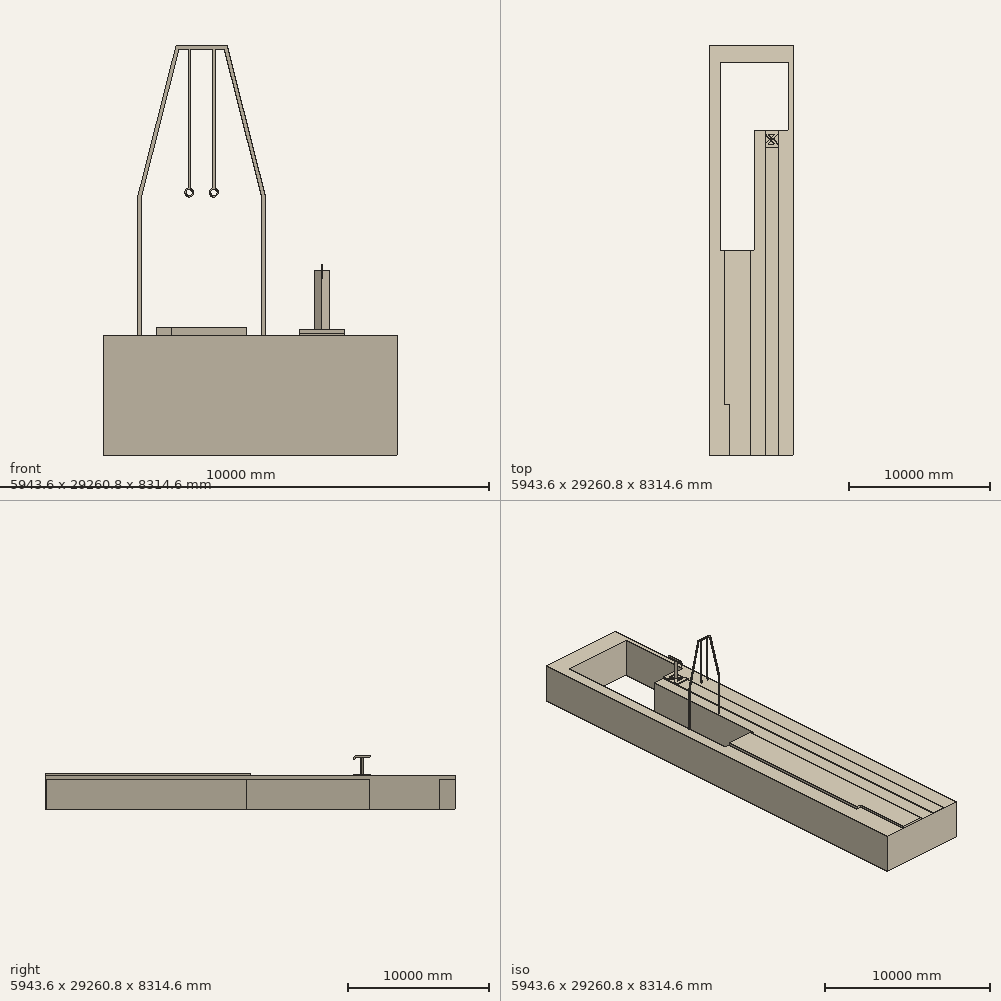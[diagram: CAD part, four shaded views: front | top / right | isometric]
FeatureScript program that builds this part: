
annotation { "Feature Type Name" : "Feature", "Feature Type Description" : "" }
export const myFeature = defineFeature(function(context is Context, id is Id, definition is map)
    precondition{}
    {
        {
            var Q0;
            Q0=qCreatedBy(makeId("Top.planeOp"),FACE);
            var sketch = newSketch(context, id + "F0", { "sketchPlane" : qUnion([Q0])});
            skLineSegment(sketch, "E0.bottom", {"start": v(-10972.8, 14630.4) * mm, "end": v(10972.8, 14630.4) * mm});
            skLineSegment(sketch, "E0.top", {"start": v(-10972.8, -14630.4) * mm, "end": v(10972.8, -14630.4) * mm});
            skLineSegment(sketch, "E0.left", {"start": v(-10972.8, 14630.4) * mm, "end": v(-10972.8, -14630.4) * mm});
            skLineSegment(sketch, "E0.right", {"start": v(10972.8, 14630.4) * mm, "end": v(10972.8, -14630.4) * mm});
            skPoint(sketch, "E0.middle", {"position": v(0, 0) * mm});
            skLineSegment(sketch, "E1", {"start": v(-10210.8, -14630.4) * mm, "end": v(-10210.8, 14630.4) * mm});
            skLineSegment(sketch, "E2", {"start": v(-7772.4, 0) * mm, "end": v(-7772.4, -14630.4) * mm});
            skLineSegment(sketch, "E3", {"start": v(-7010.4, -14630.4) * mm, "end": v(-7010.4, 0) * mm});
            skLineSegment(sketch, "E4", {"start": v(-7772.4, 0) * mm, "end": v(-9601.2, 0) * mm});
            skLineSegment(sketch, "E5", {"start": v(-9601.2, 0) * mm, "end": v(-9601.2, -10972.8) * mm});
            skLineSegment(sketch, "E6", {"start": v(-9601.2, -10972.8) * mm, "end": v(-8991.6, -10972.8) * mm});
            skLineSegment(sketch, "E7", {"start": v(-8991.6, -10972.8) * mm, "end": v(-8991.6, -14630.4) * mm});
            skLineSegment(sketch, "E8.bottom", {"start": v(-5334, 8534.4) * mm, "end": v(-7772.4, 8534.4) * mm});
            skLineSegment(sketch, "E8.top", {"start": v(-5334, 13411.2) * mm, "end": v(-7772.4, 13411.2) * mm});
            skLineSegment(sketch, "E8.left", {"start": v(-5334, 8534.4) * mm, "end": v(-5334, 13411.2) * mm});
            skLineSegment(sketch, "E8.right", {"start": v(-7772.4, 8534.4) * mm, "end": v(-7772.4, 13411.2) * mm});
            skPoint(sketch, "E8.middle", {"position": v(-6553.2, 10972.8) * mm});
            skLineSegment(sketch, "E9", {"start": v(-7772.4, 8534.4) * mm, "end": v(-7772.4, 0) * mm});
            skLineSegment(sketch, "E10", {"start": v(-5334, 8534.4) * mm, "end": v(-5334, -14630.4) * mm});
            skLineSegment(sketch, "E11", {"start": v(-5029.2, 14630.4) * mm, "end": v(-5029.2, -14630.4) * mm});
            skLineSegment(sketch, "E12", {"start": v(-6553.2, 8534.4) * mm, "end": v(-6553.2, -14630.4) * mm, "construction": true});
            skLineSegment(sketch, "E13", {"start": v(-6096, 8534.4) * mm, "end": v(-6096, -14630.4) * mm, "construction": true});
            skLineSegment(sketch, "E14", {"start": v(-7010.4, 8534.4) * mm, "end": v(-7010.4, -14630.4) * mm, "construction": true});
            skLineSegment(sketch, "E15", {"start": v(-10210.8, 3048) * mm, "end": v(-7772.4, 3048) * mm, "construction": true});
            skLineSegment(sketch, "E16", {"start": v(-10210.8, 5486.4) * mm, "end": v(-7772.4, 5486.4) * mm, "construction": true});
            skSolve(sketch);
        }
        {
            var Q0;
            Q0=qCreatedBy(makeId("Top.planeOp"),FACE);
            var sketch = newSketch(context, id + "F1", { "sketchPlane" : qUnion([Q0])});
            skLineSegment(sketch, "E17", {"start": v(-5029.2, -14630.4) * mm, "end": v(-5029.2, 14630.4) * mm});
            skLineSegment(sketch, "E18", {"start": v(-5029.2, 14630.4) * mm, "end": v(-10972.8, 14630.4) * mm});
            skLineSegment(sketch, "E19", {"start": v(-10972.8, 14630.4) * mm, "end": v(-10972.8, -14630.4) * mm});
            skLineSegment(sketch, "E20", {"start": v(-10972.8, -14630.4) * mm, "end": v(-5029.2, -14630.4) * mm});
            skLineSegment(sketch, "E21", {"start": v(-5334, 13411.2) * mm, "end": v(-5334, 8534.4) * mm});
            skLineSegment(sketch, "E22", {"start": v(-5334, 8534.4) * mm, "end": v(-7772.4, 8534.4) * mm});
            skLineSegment(sketch, "E23", {"start": v(-7772.4, 8534.4) * mm, "end": v(-7772.4, 0) * mm});
            skLineSegment(sketch, "E24", {"start": v(-7772.4, 0) * mm, "end": v(-10210.8, 0) * mm});
            skLineSegment(sketch, "E25", {"start": v(-10210.8, 0) * mm, "end": v(-10210.8, 13411.2) * mm});
            skLineSegment(sketch, "E26", {"start": v(-10210.8, 13411.2) * mm, "end": v(-5334, 13411.2) * mm});
            skSolve(sketch);
        }
        {
            var Q0;
            Q0 = qSketchRegion(id + "F1", true);
            extrude(context, id + "F2", {"entities" : qUnion([Q0]), "depth" : 2438.4 * mm});
        }
        {
            var Q0;
            Q0=makeQuery(id+"F2.opExtrude","SWEPT_FACE",FACE,{"disambiguationData":[OSD([sQuery(id+"F1.wireOp",EDGE,"E17")])]});
            var sketch = newSketch(context, id + "F3", { "sketchPlane" : qUnion([Q0])});
            skLineSegment(sketch, "E27.0", {"start": v(13411.2, 2438.4) * mm, "end": v(13411.2, 0) * mm, "construction": true});
            skLineSegment(sketch, "E28.0", {"start": v(8534.4, 2438.4) * mm, "end": v(8534.4, 0) * mm, "construction": true});
            skLineSegment(sketch, "E29.bottom", {"start": v(14630.4, 2133.6) * mm, "end": v(13462, 2133.6) * mm});
            skLineSegment(sketch, "E29.top", {"start": v(14630.4, 0) * mm, "end": v(13462, 0) * mm});
            skLineSegment(sketch, "E29.left", {"start": v(14630.4, 2133.6) * mm, "end": v(14630.4, 0) * mm});
            skLineSegment(sketch, "E29.right", {"start": v(13462, 2133.6) * mm, "end": v(13462, 0) * mm});
            skLineSegment(sketch, "E30.bottom", {"start": v(8483.6, 0) * mm, "end": v(-14528.8, 0) * mm});
            skLineSegment(sketch, "E30.top", {"start": v(8483.6, 2133.6) * mm, "end": v(-14528.8, 2133.6) * mm});
            skLineSegment(sketch, "E30.left", {"start": v(8483.6, 0) * mm, "end": v(8483.6, 2133.6) * mm});
            skLineSegment(sketch, "E30.right", {"start": v(-14528.8, 0) * mm, "end": v(-14528.8, 2133.6) * mm});
            skSolve(sketch);
        }
        {
            var Q0;
            Q0 = qSketchRegion(id + "F3", true);
            extrude(context, id + "F4", {"entities" : qUnion([Q0]), "operationType" : NewBodyOperationType.REMOVE, "oppositeDirection" : true, "depth" : 2362.2 * mm});
        }
        {
            var Q0;
            Q0=makeQuery(id+"F4.boolean.opBoolean","COPY",FACE,{"derivedFrom":makeQuery(id+"F4.opExtrude","CAP_FACE",FACE,{"disambiguationData":[OSD([sQuery(id+"F3.wireOp",EDGE,"E30.bottom"),sQuery(id+"F3.wireOp",EDGE,"E30.top"),sQuery(id+"F3.wireOp",EDGE,"E30.left"),sQuery(id+"F3.wireOp",EDGE,"E30.right")])],"isStart":false})});
            var sketch = newSketch(context, id + "F5", { "sketchPlane" : qUnion([Q0])});
            skLineSegment(sketch, "E31.bottom", {"start": v(-14528.8, 2133.6) * mm, "end": v(-304.8, 2133.6) * mm});
            skLineSegment(sketch, "E31.top", {"start": v(-14528.8, 0) * mm, "end": v(-304.8, 0) * mm});
            skLineSegment(sketch, "E31.left", {"start": v(-14528.8, 2133.6) * mm, "end": v(-14528.8, 0) * mm});
            skLineSegment(sketch, "E31.right", {"start": v(-304.8, 2133.6) * mm, "end": v(-304.8, 0) * mm});
            skSolve(sketch);
        }
        {
            var Q0;
            Q0 = qSketchRegion(id + "F5", true);
            extrude(context, id + "F6", {"entities" : qUnion([Q0]), "operationType" : NewBodyOperationType.REMOVE, "oppositeDirection" : true, "depth" : 2743.2 * mm});
        }
        {
            var Q0;
            Q0=makeQuery(id+"F2.opExtrude","CAP_FACE",FACE,{"disambiguationData":[OSD([sQuery(id+"F1.wireOp",EDGE,"E17"),sQuery(id+"F1.wireOp",EDGE,"E18"),sQuery(id+"F1.wireOp",EDGE,"E19"),sQuery(id+"F1.wireOp",EDGE,"E20"),sQuery(id+"F1.wireOp",EDGE,"E21"),sQuery(id+"F1.wireOp",EDGE,"E22"),sQuery(id+"F1.wireOp",EDGE,"E23"),sQuery(id+"F1.wireOp",EDGE,"E24"),sQuery(id+"F1.wireOp",EDGE,"E25"),sQuery(id+"F1.wireOp",EDGE,"E26")])],"isStart":false});
            var sketch = newSketch(context, id + "F7", { "sketchPlane" : qUnion([Q0])});
            skLineSegment(sketch, "E32.bottom", {"start": v(-7010.4, 8534.4) * mm, "end": v(-6096, 8534.4) * mm});
            skLineSegment(sketch, "E32.top", {"start": v(-7010.4, -14630.4) * mm, "end": v(-6096, -14630.4) * mm});
            skLineSegment(sketch, "E32.left", {"start": v(-7010.4, 8534.4) * mm, "end": v(-7010.4, -14630.4) * mm});
            skLineSegment(sketch, "E32.right", {"start": v(-6096, 8534.4) * mm, "end": v(-6096, -14630.4) * mm});
            skSolve(sketch);
        }
        {
            var Q0;
            Q0 = qSketchRegion(id + "F7", true);
            extrude(context, id + "F8", {"entities" : qUnion([Q0]), "depth" : 34.92 * mm});
        }
        {
            var Q0;
            Q0=makeQuery(id+"F8.opExtrude","CAP_FACE",FACE,{"disambiguationData":[OSD([sQuery(id+"F7.wireOp",EDGE,"E32.bottom"),sQuery(id+"F7.wireOp",EDGE,"E32.top"),sQuery(id+"F7.wireOp",EDGE,"E32.left"),sQuery(id+"F7.wireOp",EDGE,"E32.right")])],"isStart":false});
            var sketch = newSketch(context, id + "F9", { "sketchPlane" : qUnion([Q0])});
            skLineSegment(sketch, "E33.bottom", {"start": v(-7010.4, 8534.4) * mm, "end": v(-6096, 8534.4) * mm});
            skLineSegment(sketch, "E33.top", {"start": v(-7010.4, 7334.4) * mm, "end": v(-6096, 7334.4) * mm});
            skLineSegment(sketch, "E33.left", {"start": v(-7010.4, 8534.4) * mm, "end": v(-7010.4, 8302.15) * mm});
            skLineSegment(sketch, "E33.right", {"start": v(-6096, 8534.4) * mm, "end": v(-6096, 8302.15) * mm});
            skLineSegment(sketch, "E34", {"start": v(-7010.4, 8302.15) * mm, "end": v(-6698.52, 7934.4) * mm});
            skPoint(sketch, "E34.endSnap0", {"position": v(-6096, 7934.4) * mm});
            skLineSegment(sketch, "E35", {"start": v(-6698.52, 7934.4) * mm, "end": v(-7010.4, 7566.65) * mm});
            skLineSegment(sketch, "E36", {"start": v(-6096, 8302.15) * mm, "end": v(-6407.88, 7934.4) * mm});
            skLineSegment(sketch, "E37", {"start": v(-6407.88, 7934.4) * mm, "end": v(-6096, 7566.65) * mm});
            skLineSegment(sketch, "E38", {"start": v(-6698.52, 7934.4) * mm, "end": v(-7010.4, 7934.4) * mm, "construction": true});
            skLineSegment(sketch, "E39", {"start": v(-6407.88, 7934.4) * mm, "end": v(-6096, 7934.4) * mm, "construction": true});
            skLineSegment(sketch, "E40", {"start": v(-6826.71, 7566.65) * mm, "end": v(-6302.47, 7566.65) * mm});
            skLineSegment(sketch, "E41", {"start": v(-6302.47, 7566.65) * mm, "end": v(-6564.6, 7828.77) * mm});
            skLineSegment(sketch, "E42", {"start": v(-6564.6, 7828.77) * mm, "end": v(-6826.71, 7566.65) * mm});
            skLineSegment(sketch, "E43", {"start": v(-6826.71, 8302.15) * mm, "end": v(-6564.6, 8040.03) * mm});
            skLineSegment(sketch, "E44", {"start": v(-6564.6, 8040.03) * mm, "end": v(-6302.47, 8302.15) * mm});
            skLineSegment(sketch, "E45", {"start": v(-6302.47, 8302.15) * mm, "end": v(-6826.71, 8302.15) * mm});
            skLineSegment(sketch, "E46.trimOffspring", {"start": v(-7010.4, 7566.65) * mm, "end": v(-7010.4, 7334.4) * mm});
            skLineSegment(sketch, "E47.trimOffspring", {"start": v(-6096, 7566.65) * mm, "end": v(-6096, 7334.4) * mm});
            skSolve(sketch);
        }
        {
            var Q0;
            Q0 = qSketchRegion(id + "F9", true);
            extrude(context, id + "F10", {"entities" : qUnion([Q0]), "depth" : 76.2 * mm});
        }
        {
            var Q0;
            Q0=makeQuery(id+"F10.opExtrude","CAP_FACE",FACE,{"disambiguationData":[OSD([sQuery(id+"F9.wireOp",EDGE,"E33.bottom"),sQuery(id+"F9.wireOp",EDGE,"E33.top"),sQuery(id+"F9.wireOp",EDGE,"E33.left"),sQuery(id+"F9.wireOp",EDGE,"E33.right"),sQuery(id+"F9.wireOp",EDGE,"E34"),sQuery(id+"F9.wireOp",EDGE,"E35"),sQuery(id+"F9.wireOp",EDGE,"E36"),sQuery(id+"F9.wireOp",EDGE,"E37"),sQuery(id+"F9.wireOp",EDGE,"E40"),sQuery(id+"F9.wireOp",EDGE,"E41"),sQuery(id+"F9.wireOp",EDGE,"E42"),sQuery(id+"F9.wireOp",EDGE,"E43"),sQuery(id+"F9.wireOp",EDGE,"E44"),sQuery(id+"F9.wireOp",EDGE,"E45"),sQuery(id+"F9.wireOp",EDGE,"E46.trimOffspring"),sQuery(id+"F9.wireOp",EDGE,"E47.trimOffspring")])],"isStart":false});
            var sketch = newSketch(context, id + "F11", { "sketchPlane" : qUnion([Q0])});
            skLineSegment(sketch, "E48", {"start": v(-6698.52, 7934.4) * mm, "end": v(-6564.6, 8040.03) * mm});
            skLineSegment(sketch, "E49", {"start": v(-6564.6, 8040.03) * mm, "end": v(-6407.88, 7934.4) * mm});
            skLineSegment(sketch, "E50", {"start": v(-6407.88, 7934.4) * mm, "end": v(-6564.6, 7828.77) * mm});
            skLineSegment(sketch, "E51", {"start": v(-6564.6, 7828.77) * mm, "end": v(-6698.52, 7934.4) * mm});
            skSolve(sketch);
        }
        {
            var Q0;
            Q0 = qSketchRegion(id + "F11", true);
            extrude(context, id + "F12", {"entities" : qUnion([Q0]), "operationType" : NewBodyOperationType.ADD, "depth" : 1200 * mm});
        }
        {
            var Q0;
            Q0=makeQuery(id+"F10.opExtrude","SWEPT_FACE",FACE,{"disambiguationData":[OSD([sQuery(id+"F9.wireOp",EDGE,"E33.left")])]});
            var Q1;
            Q1=makeQuery(id+"F10.opExtrude","SWEPT_FACE",FACE,{"disambiguationData":[OSD([sQuery(id+"F9.wireOp",EDGE,"E33.right")])]});
            cPlane(context, id + "F13", {"entities" : qUnion([Q0, Q1]), "cplaneType" : CPlaneType.MID_PLANE, "offset" : 25.4 * mm, "width" : 152.4 * mm, "height" : 152.4 * mm});
        }
        {
            var Q0;
            Q0=qCreatedBy(id+"F13.planeOp",FACE);
            var sketch = newSketch(context, id + "F14", { "sketchPlane" : qUnion([Q0])});
            skLineSegment(sketch, "E52", {"start": v(-8534.4, 3749.53) * mm, "end": v(-7652.6, 3749.53) * mm});
            skLineSegment(sketch, "E53", {"start": v(-7334.4, 2549.53) * mm, "end": v(-7334.4, 3749.53) * mm, "construction": true});
            skLineSegment(sketch, "E54", {"start": v(-8534.4, 3749.53) * mm, "end": v(-8534.4, 3880.04) * mm});
            skLineSegment(sketch, "E55", {"start": v(-8534.4, 3880.04) * mm, "end": v(-7652.6, 3880.04) * mm});
            skArc(sketch, "E56", {"start": v(-7464.92, 3561.85) * mm, "mid": v(-7519.89, 3694.56) * mm, "end": v(-7652.6, 3749.53) * mm});
            skArc(sketch, "E57", {"start": v(-7334.4, 3561.85) * mm, "mid": v(-7427.6, 3786.85) * mm, "end": v(-7652.6, 3880.04) * mm});
            skLineSegment(sketch, "E58", {"start": v(-7464.92, 3561.85) * mm, "end": v(-7334.4, 3561.85) * mm});
            skSolve(sketch);
        }
        {
            var Q0;
            Q0 = qSketchRegion(id + "F14", true);
            extrude(context, id + "F15", {"entities" : qUnion([Q0]), "operationType" : NewBodyOperationType.ADD, "depth" : 95 / 20 * mm, "hasSecondDirection" : true, "secondDirectionOppositeDirection" : true, "secondDirectionDepth" : 95 / 20 * mm});
        }
        {
            var Q0;
            Q0=makeQuery(id+"F2.opExtrude","CAP_FACE",FACE,{"disambiguationData":[OSD([sQuery(id+"F1.wireOp",EDGE,"E17"),sQuery(id+"F1.wireOp",EDGE,"E18"),sQuery(id+"F1.wireOp",EDGE,"E19"),sQuery(id+"F1.wireOp",EDGE,"E20"),sQuery(id+"F1.wireOp",EDGE,"E21"),sQuery(id+"F1.wireOp",EDGE,"E22"),sQuery(id+"F1.wireOp",EDGE,"E23"),sQuery(id+"F1.wireOp",EDGE,"E24"),sQuery(id+"F1.wireOp",EDGE,"E25"),sQuery(id+"F1.wireOp",EDGE,"E26")])],"isStart":false});
            var sketch = newSketch(context, id + "F16", { "sketchPlane" : qUnion([Q0])});
            skLineSegment(sketch, "E59", {"start": v(-9906, 0) * mm, "end": v(-7772.4, 0) * mm});
            skLineSegment(sketch, "E60", {"start": v(-8077.2, 0) * mm, "end": v(-8077.2, -14630.4) * mm});
            skLineSegment(sketch, "E61", {"start": v(-8077.2, -14630.4) * mm, "end": v(-9601.2, -14630.4) * mm});
            skLineSegment(sketch, "E62", {"start": v(-9906, 0) * mm, "end": v(-9906, -10972.8) * mm});
            skLineSegment(sketch, "E63", {"start": v(-9906, -10972.8) * mm, "end": v(-9601.2, -10972.8) * mm});
            skLineSegment(sketch, "E64", {"start": v(-9601.2, -10972.8) * mm, "end": v(-9601.2, -14630.4) * mm});
            skSolve(sketch);
        }
        {
            var Q0;
            Q0 = qSketchRegion(id + "F16", true);
            extrude(context, id + "F17", {"entities" : qUnion([Q0]), "depth" : 152.4 * mm});
        }
        {
            var Q0;
            Q0=makeQuery(id+"F2.opExtrude","SWEPT_FACE",FACE,{"disambiguationData":[OSD([sQuery(id+"F1.wireOp",EDGE,"E24")])]});
            var Q1;
            Q1=sQuery(id+"F0.wireOp",VERTEX,"E15.end");
            cPlane(context, id + "F18", {"entities" : qUnion([Q0, Q1]), "cplaneType" : CPlaneType.PLANE_POINT, "offset" : 25.4 * mm, "width" : 152.4 * mm, "height" : 152.4 * mm});
        }
        {
            var Q0;
            Q0=qCreatedBy(id+"F18.planeOp",FACE);
            var sketch = newSketch(context, id + "F19", { "sketchPlane" : qUnion([Q0])});
            skLineSegment(sketch, "E65.0", {"start": v(7772.4, 2438.4) * mm, "end": v(10210.8, 2438.4) * mm, "construction": true});
            skLineSegment(sketch, "E66", {"start": v(8991.6, 2438.4) * mm, "end": v(8991.6, 8238.4) * mm, "construction": true});
            skLineSegment(sketch, "E67", {"start": v(10210.8, 2438.4) * mm, "end": v(10210.8, 5238.4) * mm});
            skLineSegment(sketch, "E68", {"start": v(10210.8, 5238.4) * mm, "end": v(9448.8, 8238.4) * mm});
            skLineSegment(sketch, "E69", {"start": v(9448.8, 8238.4) * mm, "end": v(8534.4, 8238.4) * mm});
            skLineSegment(sketch, "E70", {"start": v(8534.4, 8238.4) * mm, "end": v(7772.4, 5238.4) * mm});
            skLineSegment(sketch, "E71", {"start": v(7772.4, 5238.4) * mm, "end": v(7772.4, 2438.4) * mm});
            skLineSegment(sketch, "E72.0", {"start": v(7696.2, 5247.93) * mm, "end": v(7696.2, 2438.4) * mm});
            skLineSegment(sketch, "E72.1", {"start": v(10287, 2438.4) * mm, "end": v(10287, 5247.93) * mm});
            skLineSegment(sketch, "E72.2", {"start": v(10287, 5247.93) * mm, "end": v(9508.06, 8314.6) * mm});
            skLineSegment(sketch, "E72.3", {"start": v(9508.06, 8314.6) * mm, "end": v(8475.14, 8314.6) * mm});
            skLineSegment(sketch, "E72.4", {"start": v(8475.14, 8314.6) * mm, "end": v(7696.2, 5247.93) * mm});
            skLineSegment(sketch, "E73", {"start": v(10287, 2438.4) * mm, "end": v(10210.8, 2438.4) * mm});
            skLineSegment(sketch, "E74", {"start": v(7696.2, 2438.4) * mm, "end": v(7772.4, 2438.4) * mm});
            skSolve(sketch);
        }
        {
            var Q0;
            Q0=makeQuery(id+"F19.imprint","IMPRINT",FACE,{"disambiguationData":[TD([[makeQuery(id+"F19.imprint","IMPRINT",EDGE,{"derivedFrom":sQuery(id+"F19.wireOp",EDGE,"E67")}),-1.0]])]});
            extrude(context, id + "F20", {"entities" : qUnion([Q0]), "depth" : 50.8 * mm});
        }
        {
            var Q0;
            Q0=makeQuery(id+"F20.opExtrude","CAP_FACE",FACE,{"disambiguationData":[OSD([sQuery(id+"F19.wireOp",EDGE,"E67"),sQuery(id+"F19.wireOp",EDGE,"E68"),sQuery(id+"F19.wireOp",EDGE,"E69"),sQuery(id+"F19.wireOp",EDGE,"E70"),sQuery(id+"F19.wireOp",EDGE,"E71"),sQuery(id+"F19.wireOp",EDGE,"E72.0"),sQuery(id+"F19.wireOp",EDGE,"E72.1"),sQuery(id+"F19.wireOp",EDGE,"E72.2"),sQuery(id+"F19.wireOp",EDGE,"E72.3"),sQuery(id+"F19.wireOp",EDGE,"E72.4"),sQuery(id+"F19.wireOp",EDGE,"E73"),sQuery(id+"F19.wireOp",EDGE,"E74")])],"isStart":true});
            var sketch = newSketch(context, id + "F21", { "sketchPlane" : qUnion([Q0])});
            skLineSegment(sketch, "E75", {"start": v(-10210.8, 5238.4) * mm, "end": v(-7772.4, 5238.4) * mm, "construction": true});
            skLineSegment(sketch, "E76", {"start": v(-8991.6, 5238.4) * mm, "end": v(-8991.6, 8238.4) * mm, "construction": true});
            skCircle(sketch, "E77", {"center": v(-8741.6, 5328.4) * mm, "radius": 90 * mm});
            skCircle(sketch, "E78", {"center": v(-9241.6, 5328.4) * mm, "radius": 90 * mm});
            skCircle(sketch, "E79", {"center": v(-8741.6, 5328.4) * mm, "radius": 64.6 * mm});
            skCircle(sketch, "E80", {"center": v(-9241.6, 5328.4) * mm, "radius": 64.6 * mm});
            skLineSegment(sketch, "E81", {"start": v(-9241.6, 5418.4) * mm, "end": v(-9241.6, 8238.4) * mm, "construction": true});
            skLineSegment(sketch, "E82", {"start": v(-8741.6, 5418.4) * mm, "end": v(-8741.6, 8238.4) * mm, "construction": true});
            skLineSegment(sketch, "E83", {"start": v(-9267, 8238.4) * mm, "end": v(-9267, 5414.74) * mm});
            skLineSegment(sketch, "E84", {"start": v(-9216.2, 5414.74) * mm, "end": v(-9216.2, 8238.4) * mm});
            skLineSegment(sketch, "E85", {"start": v(-8716.2, 8238.4) * mm, "end": v(-8716.2, 5414.74) * mm});
            skLineSegment(sketch, "E86", {"start": v(-8767, 8238.4) * mm, "end": v(-8767, 5414.74) * mm});
            skLineSegment(sketch, "E87", {"start": v(-9267, 8238.4) * mm, "end": v(-9216.2, 8238.4) * mm});
            skLineSegment(sketch, "E88", {"start": v(-8767, 8238.4) * mm, "end": v(-8716.2, 8238.4) * mm});
            skSolve(sketch);
        }
        {
            var Q0;
            Q0 = qSketchRegion(id + "F21", true);
            extrude(context, id + "F22", {"entities" : qUnion([Q0]), "operationType" : NewBodyOperationType.ADD, "oppositeDirection" : true, "depth" : 25.4 * mm});
        }
    });
